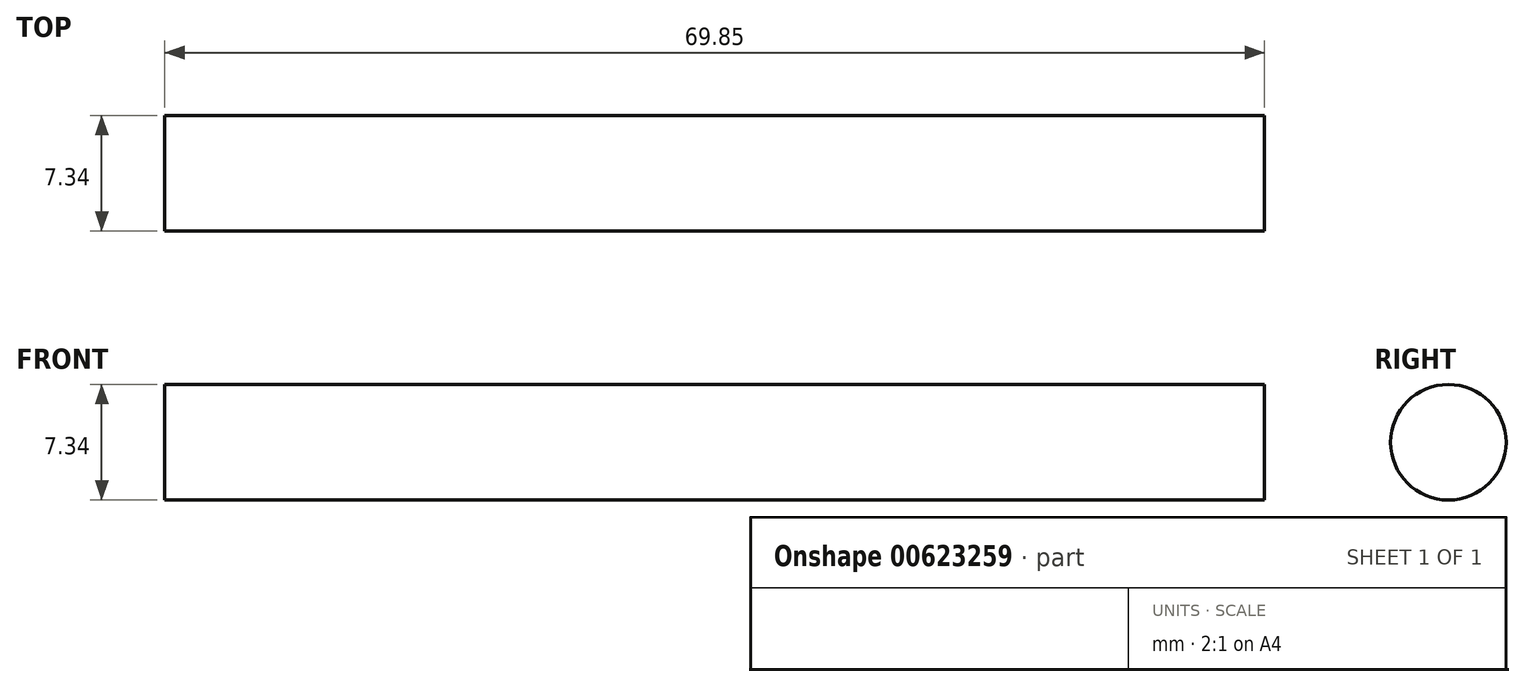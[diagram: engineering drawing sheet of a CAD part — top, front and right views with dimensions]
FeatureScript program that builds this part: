
annotation { "Feature Type Name" : "Feature", "Feature Type Description" : "" }
export const myFeature = defineFeature(function(context is Context, id is Id, definition is map)
    precondition{}
    {
        {
            var Q0;
            Q0=qCreatedBy(makeId("Right.planeOp"),FACE);
            var sketch = newSketch(context, id + "F0", { "sketchPlane" : qUnion([Q0])});
            skCircle(sketch, "E0", {"center": v(0, 0) * mm, "radius": 3.67 * mm});
            skSolve(sketch);
        }
        {
            var Q0;
            Q0 = qSketchRegion(id + "F0", true);
            extrude(context, id + "F1", {"entities" : qUnion([Q0]), "depth" : 69.85 * mm, "offsetDistance" : 25.4 * mm});
        }
    });
